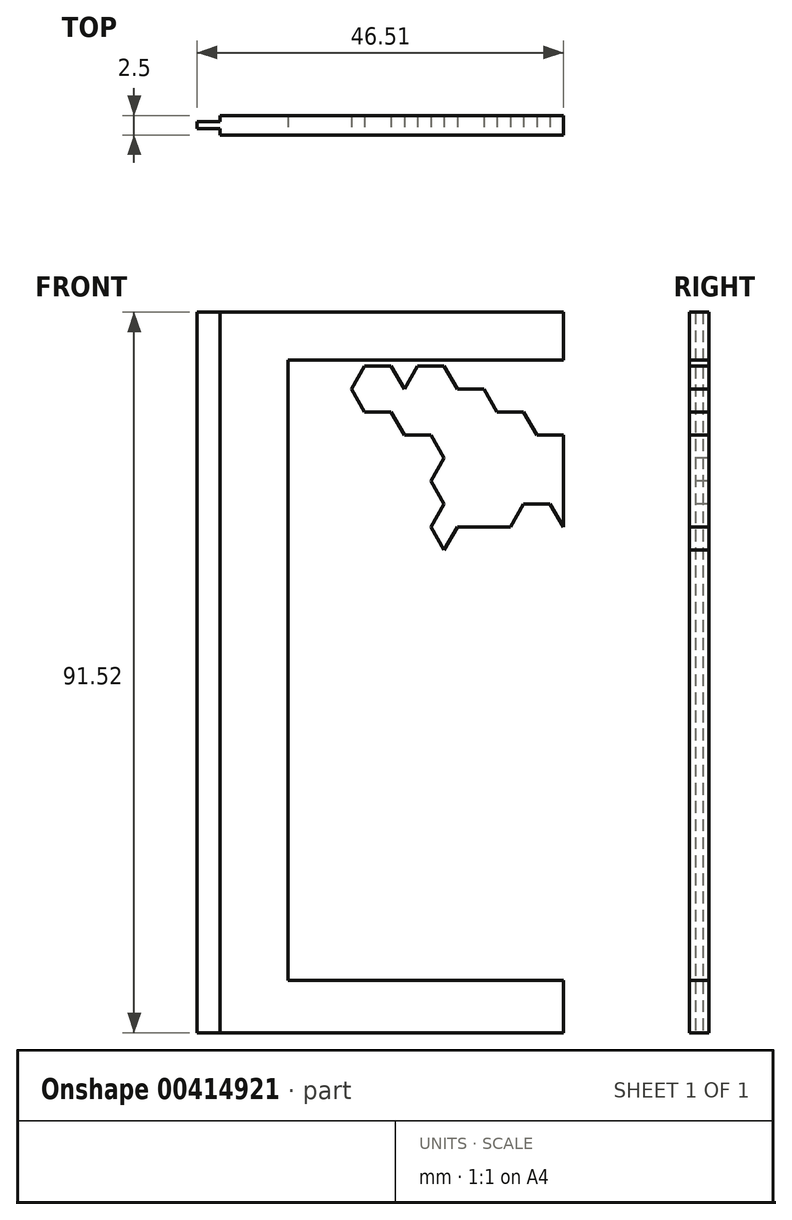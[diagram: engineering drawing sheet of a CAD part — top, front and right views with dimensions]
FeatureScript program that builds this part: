
annotation { "Feature Type Name" : "Feature", "Feature Type Description" : "" }
export const myFeature = defineFeature(function(context is Context, id is Id, definition is map)
    precondition{}
    {
        {
            var Q0;
            Q0=qCreatedBy(makeId("Front.planeOp"),FACE);
            var sketch = newSketch(context, id + "F0", { "sketchPlane" : qUnion([Q0])});
            skLineSegment(sketch, "E0.bottom", {"start": v(-43.61, 45.76) * mm, "end": v(0, 45.76) * mm});
            skLineSegment(sketch, "E0.top", {"start": v(-43.61, -45.76) * mm, "end": v(0, -45.76) * mm});
            skLineSegment(sketch, "E0.left", {"start": v(-43.61, 45.76) * mm, "end": v(-43.61, -45.76) * mm});
            skLineSegment(sketch, "E0.right", {"start": v(0, 45.76) * mm, "end": v(0, -45.76) * mm});
            skSolve(sketch);
        }
        {
            var Q0;
            Q0=makeQuery(id+"F0.imprint","IMPRINT",FACE,{"disambiguationData":[TD([[makeQuery(id+"F0.imprint","IMPRINT",EDGE,{"derivedFrom":sQuery(id+"F0.wireOp",EDGE,"E0.bottom")}),-1.0]])]});
            extrude(context, id + "F1", {"entities" : qUnion([Q0]), "oppositeDirection" : true, "depth" : 2.5 * mm});
        }
        {
            var Q0;
            Q0=makeQuery(id+"F1.opExtrude","SWEPT_FACE",FACE,{"disambiguationData":[OSD([sQuery(id+"F0.wireOp",EDGE,"E0.left")])]});
            var sketch = newSketch(context, id + "F2", { "sketchPlane" : qUnion([Q0])});
            skLineSegment(sketch, "E1.bottom", {"start": v(-0.8, 45.76) * mm, "end": v(-1.7, 45.76) * mm});
            skLineSegment(sketch, "E1.top", {"start": v(-0.8, -45.76) * mm, "end": v(-1.7, -45.76) * mm});
            skLineSegment(sketch, "E1.left", {"start": v(-0.8, 45.76) * mm, "end": v(-0.8, -45.76) * mm});
            skLineSegment(sketch, "E1.right", {"start": v(-1.7, 45.76) * mm, "end": v(-1.7, -45.76) * mm});
            skLineSegment(sketch, "E2", {"start": v(-2.5, -45.76) * mm, "end": v(-1.7, -45.76) * mm, "construction": true});
            skLineSegment(sketch, "E3", {"start": v(-0.8, -45.76) * mm, "end": v(0, -45.76) * mm, "construction": true});
            skSolve(sketch);
        }
        {
            var Q0;
            Q0=makeQuery(id+"F2.imprint","IMPRINT",FACE,{"disambiguationData":[TD([[makeQuery(id+"F2.imprint","IMPRINT",EDGE,{"derivedFrom":sQuery(id+"F2.wireOp",EDGE,"E1.bottom")}),-1.0]])]});
            extrude(context, id + "F3", {"entities" : qUnion([Q0]), "operationType" : NewBodyOperationType.ADD, "depth" : 2.9 * mm});
        }
        {
            var Q0;
            Q0=makeQuery(id+"F1.opExtrude","CAP_FACE",FACE,{"disambiguationData":[OSD([sQuery(id+"F0.wireOp",EDGE,"E0.bottom"),sQuery(id+"F0.wireOp",EDGE,"E0.top"),sQuery(id+"F0.wireOp",EDGE,"E0.left"),sQuery(id+"F0.wireOp",EDGE,"E0.right")])],"isStart":true});
            var sketch = newSketch(context, id + "F4", { "sketchPlane" : qUnion([Q0])});
            skLineSegment(sketch, "E4.bottom", {"start": v(0, 39.65) * mm, "end": v(-34.96, 39.65) * mm});
            skLineSegment(sketch, "E4.top", {"start": v(0, -39.14) * mm, "end": v(-34.96, -39.14) * mm});
            skLineSegment(sketch, "E4.left", {"start": v(0, 39.65) * mm, "end": v(0, -39.14) * mm});
            skLineSegment(sketch, "E4.right", {"start": v(-34.96, 39.65) * mm, "end": v(-34.96, -39.14) * mm});
            skLineSegment(sketch, "E5", {"start": v(0, 24.32) * mm, "end": v(0, 21.4) * mm});
            skLineSegment(sketch, "E6", {"start": v(-1.68, 21.4) * mm, "end": v(0, 24.32) * mm});
            skLineSegment(sketch, "E7.MirrorCS", {"start": v(0, 18.49) * mm, "end": v(0, 21.4) * mm});
            skLineSegment(sketch, "E8.MirrorCS", {"start": v(0, 3.16) * mm, "end": v(0, 81.95) * mm});
            skLineSegment(sketch, "E9.MirrorCS", {"start": v(-1.68, 21.4) * mm, "end": v(0, 18.49) * mm});
            skLineSegment(sketch, "E10.MirrorCS", {"start": v(-1.68, 21.4) * mm, "end": v(-5.05, 21.4) * mm});
            skLineSegment(sketch, "E11.MirrorCS", {"start": v(-5.05, 21.4) * mm, "end": v(-2.53, 22.86) * mm});
            skLineSegment(sketch, "E12.MirrorCS", {"start": v(0, 24.32) * mm, "end": v(-2.53, 22.86) * mm});
            skLineSegment(sketch, "E13.MirrorCS", {"start": v(-3.37, 24.32) * mm, "end": v(-5.05, 21.4) * mm});
            skLineSegment(sketch, "E14.MirrorCS", {"start": v(-3.37, 24.32) * mm, "end": v(0, 24.32) * mm});
            skLineSegment(sketch, "E15.MirrorCS", {"start": v(-3.37, 24.32) * mm, "end": v(-5.05, 27.24) * mm});
            skLineSegment(sketch, "E16.MirrorCS", {"start": v(-5.05, 27.24) * mm, "end": v(-2.53, 25.78) * mm});
            skLineSegment(sketch, "E17.MirrorCS", {"start": v(0, 24.32) * mm, "end": v(-2.53, 25.78) * mm});
            skLineSegment(sketch, "E18.MirrorCS", {"start": v(-1.68, 27.24) * mm, "end": v(0, 24.32) * mm});
            skLineSegment(sketch, "E19.MirrorCS", {"start": v(-1.68, 27.24) * mm, "end": v(-5.05, 27.24) * mm});
            skLineSegment(sketch, "E20.MirrorCS", {"start": v(-1.68, 27.24) * mm, "end": v(0, 30.16) * mm});
            skLineSegment(sketch, "E21.MirrorCS", {"start": v(0, 45.49) * mm, "end": v(0, -33.3) * mm});
            skLineSegment(sketch, "E22.MirrorCS", {"start": v(0, 30.16) * mm, "end": v(0, 27.24) * mm});
            skLineSegment(sketch, "E23.MirrorCS", {"start": v(-5.05, 27.24) * mm, "end": v(-5.05, 24.32) * mm});
            skLineSegment(sketch, "E24.MirrorCS", {"start": v(-5.05, 21.4) * mm, "end": v(-5.05, 24.32) * mm});
            skLineSegment(sketch, "E25.MirrorCS", {"start": v(-6.74, 24.32) * mm, "end": v(-5.05, 27.24) * mm});
            skLineSegment(sketch, "E26.MirrorCS", {"start": v(-6.74, 24.32) * mm, "end": v(-5.05, 21.4) * mm});
            skLineSegment(sketch, "E27.MirrorCS", {"start": v(-6.74, 24.32) * mm, "end": v(-10.1, 24.32) * mm});
            skLineSegment(sketch, "E28.MirrorCS", {"start": v(-10.1, 24.32) * mm, "end": v(-7.58, 25.78) * mm});
            skLineSegment(sketch, "E29.MirrorCS", {"start": v(-5.05, 27.24) * mm, "end": v(-7.58, 25.78) * mm});
            skLineSegment(sketch, "E30.MirrorCS", {"start": v(-8.42, 27.24) * mm, "end": v(-5.05, 27.24) * mm});
            skLineSegment(sketch, "E31.MirrorCS", {"start": v(-5.05, 27.24) * mm, "end": v(-7.58, 28.7) * mm});
            skLineSegment(sketch, "E32.MirrorCS", {"start": v(-10.1, 30.16) * mm, "end": v(-7.58, 28.7) * mm});
            skLineSegment(sketch, "E33.MirrorCS", {"start": v(-6.74, 30.16) * mm, "end": v(-5.05, 27.24) * mm});
            skLineSegment(sketch, "E34.MirrorCS", {"start": v(-6.74, 30.16) * mm, "end": v(-10.1, 30.16) * mm});
            skLineSegment(sketch, "E35.MirrorCS", {"start": v(-10.1, 30.16) * mm, "end": v(-10.1, 27.24) * mm});
            skLineSegment(sketch, "E36.MirrorCS", {"start": v(-10.1, 24.32) * mm, "end": v(-10.1, 27.24) * mm});
            skLineSegment(sketch, "E37.MirrorCS", {"start": v(-8.42, 27.24) * mm, "end": v(-10.1, 24.32) * mm});
            skLineSegment(sketch, "E38.MirrorCS", {"start": v(-8.42, 27.24) * mm, "end": v(-10.1, 30.16) * mm});
            skLineSegment(sketch, "E39.MirrorCS", {"start": v(-11.79, 27.24) * mm, "end": v(-15.15, 27.24) * mm});
            skLineSegment(sketch, "E40.MirrorCS", {"start": v(-11.79, 27.24) * mm, "end": v(-10.1, 30.16) * mm});
            skLineSegment(sketch, "E41.MirrorCS", {"start": v(-11.79, 27.24) * mm, "end": v(-10.1, 24.32) * mm});
            skLineSegment(sketch, "E42.MirrorCS", {"start": v(-15.15, 27.24) * mm, "end": v(-12.63, 28.7) * mm});
            skLineSegment(sketch, "E43.MirrorCS", {"start": v(-11.79, 33.07) * mm, "end": v(-10.1, 30.16) * mm});
            skLineSegment(sketch, "E44.MirrorCS", {"start": v(-11.79, 33.07) * mm, "end": v(-15.15, 33.07) * mm});
            skLineSegment(sketch, "E45.MirrorCS", {"start": v(-16.84, 35.99) * mm, "end": v(-15.15, 33.07) * mm});
            skLineSegment(sketch, "E46.MirrorCS", {"start": v(-16.84, 35.99) * mm, "end": v(-20.2, 35.99) * mm});
            skLineSegment(sketch, "E47.MirrorCS", {"start": v(-21.89, 33.07) * mm, "end": v(-20.2, 35.99) * mm});
            skLineSegment(sketch, "E48.MirrorCS", {"start": v(-21.89, 33.07) * mm, "end": v(-20.2, 30.16) * mm});
            skLineSegment(sketch, "E49.MirrorCS", {"start": v(-18.52, 33.07) * mm, "end": v(-20.2, 35.99) * mm});
            skLineSegment(sketch, "E50.MirrorCS", {"start": v(-18.52, 33.07) * mm, "end": v(-20.2, 30.16) * mm});
            skLineSegment(sketch, "E51.MirrorCS", {"start": v(-18.52, 33.07) * mm, "end": v(-15.15, 33.07) * mm});
            skLineSegment(sketch, "E52.MirrorCS", {"start": v(-20.2, 30.16) * mm, "end": v(-17.68, 31.61) * mm});
            skLineSegment(sketch, "E53.MirrorCS", {"start": v(-15.15, 33.07) * mm, "end": v(-17.68, 31.61) * mm});
            skLineSegment(sketch, "E54.MirrorCS", {"start": v(-16.84, 30.16) * mm, "end": v(-20.2, 30.16) * mm});
            skLineSegment(sketch, "E55.MirrorCS", {"start": v(-16.84, 30.16) * mm, "end": v(-15.15, 33.07) * mm});
            skLineSegment(sketch, "E56.MirrorCS", {"start": v(-16.84, 30.16) * mm, "end": v(-15.15, 27.24) * mm});
            skLineSegment(sketch, "E57.MirrorCS", {"start": v(-15.15, 33.07) * mm, "end": v(-15.15, 30.16) * mm});
            skLineSegment(sketch, "E58.MirrorCS", {"start": v(-15.15, 27.24) * mm, "end": v(-15.15, 30.16) * mm});
            skLineSegment(sketch, "E59.MirrorCS", {"start": v(-13.47, 30.16) * mm, "end": v(-15.15, 27.24) * mm});
            skLineSegment(sketch, "E60.MirrorCS", {"start": v(-13.47, 30.16) * mm, "end": v(-15.15, 33.07) * mm});
            skLineSegment(sketch, "E61.MirrorCS", {"start": v(-13.47, 30.16) * mm, "end": v(-10.1, 30.16) * mm});
            skLineSegment(sketch, "E62.MirrorCS", {"start": v(-10.1, 30.16) * mm, "end": v(-12.63, 28.7) * mm});
            skLineSegment(sketch, "E63.MirrorCS", {"start": v(-10.1, 30.16) * mm, "end": v(-12.63, 31.61) * mm});
            skLineSegment(sketch, "E64.MirrorCS", {"start": v(-15.15, 33.07) * mm, "end": v(-12.63, 31.61) * mm});
            skLineSegment(sketch, "E65.MirrorCS", {"start": v(-15.15, 33.07) * mm, "end": v(-17.68, 34.53) * mm});
            skLineSegment(sketch, "E66.MirrorCS", {"start": v(-20.2, 35.99) * mm, "end": v(-17.68, 34.53) * mm});
            skLineSegment(sketch, "E67.MirrorCS", {"start": v(-20.2, 35.99) * mm, "end": v(-20.2, 33.07) * mm});
            skLineSegment(sketch, "E68.MirrorCS", {"start": v(-20.2, 30.16) * mm, "end": v(-20.2, 33.07) * mm});
            skLineSegment(sketch, "E69.MirrorCS", {"start": v(-18.52, 38.9) * mm, "end": v(-20.2, 35.99) * mm});
            skLineSegment(sketch, "E70.MirrorCS", {"start": v(-18.52, 38.9) * mm, "end": v(-15.15, 38.9) * mm});
            skLineSegment(sketch, "E71.MirrorCS", {"start": v(-13.47, 35.99) * mm, "end": v(-15.15, 38.9) * mm});
            skLineSegment(sketch, "E72.MirrorCS", {"start": v(-13.47, 35.99) * mm, "end": v(-10.1, 35.99) * mm});
            skLineSegment(sketch, "E73.MirrorCS", {"start": v(-8.42, 33.07) * mm, "end": v(-10.1, 35.99) * mm});
            skLineSegment(sketch, "E74.MirrorCS", {"start": v(-8.42, 33.07) * mm, "end": v(-5.05, 33.07) * mm});
            skLineSegment(sketch, "E75.MirrorCS", {"start": v(-3.37, 30.16) * mm, "end": v(-5.05, 33.07) * mm});
            skLineSegment(sketch, "E76.MirrorCS", {"start": v(-3.37, 30.16) * mm, "end": v(0, 30.16) * mm});
            skLineSegment(sketch, "E77.MirrorCS", {"start": v(-20.2, 35.99) * mm, "end": v(-17.68, 37.45) * mm});
            skLineSegment(sketch, "E78.MirrorCS", {"start": v(-15.15, 38.9) * mm, "end": v(-17.68, 37.45) * mm});
            skLineSegment(sketch, "E79.MirrorCS", {"start": v(-16.84, 35.99) * mm, "end": v(-15.15, 38.9) * mm});
            skLineSegment(sketch, "E80.MirrorCS", {"start": v(-15.15, 38.9) * mm, "end": v(-15.15, 35.99) * mm});
            skLineSegment(sketch, "E81.MirrorCS", {"start": v(-15.15, 33.07) * mm, "end": v(-15.15, 35.99) * mm});
            skLineSegment(sketch, "E82.MirrorCS", {"start": v(-13.47, 35.99) * mm, "end": v(-15.15, 33.07) * mm});
            skLineSegment(sketch, "E83.MirrorCS", {"start": v(-15.15, 33.07) * mm, "end": v(-12.63, 34.53) * mm});
            skLineSegment(sketch, "E84.MirrorCS", {"start": v(-10.1, 35.99) * mm, "end": v(-12.63, 34.53) * mm});
            skLineSegment(sketch, "E85.MirrorCS", {"start": v(-11.79, 33.07) * mm, "end": v(-10.1, 35.99) * mm});
            skLineSegment(sketch, "E86.MirrorCS", {"start": v(-10.1, 35.99) * mm, "end": v(-10.1, 33.07) * mm});
            skLineSegment(sketch, "E87.MirrorCS", {"start": v(-10.1, 30.16) * mm, "end": v(-10.1, 33.07) * mm});
            skLineSegment(sketch, "E88.MirrorCS", {"start": v(-8.42, 33.07) * mm, "end": v(-10.1, 30.16) * mm});
            skLineSegment(sketch, "E89.MirrorCS", {"start": v(-10.1, 30.16) * mm, "end": v(-7.58, 31.61) * mm});
            skLineSegment(sketch, "E90.MirrorCS", {"start": v(-5.05, 33.07) * mm, "end": v(-7.58, 31.61) * mm});
            skLineSegment(sketch, "E91.MirrorCS", {"start": v(-6.74, 30.16) * mm, "end": v(-5.05, 33.07) * mm});
            skLineSegment(sketch, "E92.MirrorCS", {"start": v(-5.05, 33.07) * mm, "end": v(-5.05, 30.16) * mm});
            skLineSegment(sketch, "E93.MirrorCS", {"start": v(-5.05, 27.24) * mm, "end": v(-5.05, 30.16) * mm});
            skLineSegment(sketch, "E94.MirrorCS", {"start": v(-3.37, 30.16) * mm, "end": v(-5.05, 27.24) * mm});
            skLineSegment(sketch, "E95.MirrorCS", {"start": v(-5.05, 27.24) * mm, "end": v(-2.53, 28.7) * mm});
            skLineSegment(sketch, "E96.MirrorCS", {"start": v(0, 30.16) * mm, "end": v(-2.53, 28.7) * mm});
            skLineSegment(sketch, "E97.MirrorCS", {"start": v(-21.89, 33.07) * mm, "end": v(-25.26, 33.07) * mm});
            skLineSegment(sketch, "E98.MirrorCS", {"start": v(-26.94, 35.99) * mm, "end": v(-25.26, 33.07) * mm});
            skLineSegment(sketch, "E99.MirrorCS", {"start": v(-26.94, 35.99) * mm, "end": v(-25.26, 38.9) * mm});
            skLineSegment(sketch, "E100.MirrorCS", {"start": v(-25.26, 38.9) * mm, "end": v(-22.73, 37.45) * mm});
            skLineSegment(sketch, "E101.MirrorCS", {"start": v(-20.2, 35.99) * mm, "end": v(-22.73, 37.45) * mm});
            skLineSegment(sketch, "E102.MirrorCS", {"start": v(-21.89, 38.9) * mm, "end": v(-20.2, 35.99) * mm});
            skLineSegment(sketch, "E103.MirrorCS", {"start": v(-21.89, 38.9) * mm, "end": v(-25.26, 38.9) * mm});
            skLineSegment(sketch, "E104.MirrorCS", {"start": v(-25.26, 38.9) * mm, "end": v(-25.26, 35.99) * mm});
            skLineSegment(sketch, "E105.MirrorCS", {"start": v(-25.26, 33.07) * mm, "end": v(-25.26, 35.99) * mm});
            skLineSegment(sketch, "E106.MirrorCS", {"start": v(-23.57, 35.99) * mm, "end": v(-25.26, 33.07) * mm});
            skLineSegment(sketch, "E107.MirrorCS", {"start": v(-23.57, 35.99) * mm, "end": v(-20.2, 35.99) * mm});
            skLineSegment(sketch, "E108.MirrorCS", {"start": v(-20.2, 35.99) * mm, "end": v(-22.73, 34.53) * mm});
            skLineSegment(sketch, "E109.MirrorCS", {"start": v(-25.26, 33.07) * mm, "end": v(-22.73, 34.53) * mm});
            skLineSegment(sketch, "E110.MirrorCS", {"start": v(-20.2, 35.99) * mm, "end": v(-20.2, 38.9) * mm});
            skLineSegment(sketch, "E111.MirrorCS", {"start": v(-10.1, 24.32) * mm, "end": v(-10.1, 21.4) * mm});
            skLineSegment(sketch, "E112.MirrorCS", {"start": v(-10.1, 18.49) * mm, "end": v(-10.1, 21.4) * mm});
            skLineSegment(sketch, "E113.MirrorCS", {"start": v(-6.74, 18.49) * mm, "end": v(-10.1, 18.49) * mm});
            skLineSegment(sketch, "E114.MirrorCS", {"start": v(-6.74, 18.49) * mm, "end": v(-5.05, 15.57) * mm});
            skLineSegment(sketch, "E115.MirrorCS", {"start": v(-6.74, 18.49) * mm, "end": v(-5.05, 21.4) * mm});
            skLineSegment(sketch, "E116.MirrorCS", {"start": v(-5.05, 21.4) * mm, "end": v(-7.58, 19.95) * mm});
            skLineSegment(sketch, "E117.MirrorCS", {"start": v(-10.1, 18.49) * mm, "end": v(-7.58, 19.95) * mm});
            skLineSegment(sketch, "E118.MirrorCS", {"start": v(-8.42, 21.4) * mm, "end": v(-5.05, 21.4) * mm});
            skLineSegment(sketch, "E119.MirrorCS", {"start": v(-8.42, 21.4) * mm, "end": v(-10.1, 24.32) * mm});
            skLineSegment(sketch, "E120.MirrorCS", {"start": v(-8.42, 21.4) * mm, "end": v(-10.1, 18.49) * mm});
            skLineSegment(sketch, "E121.MirrorCS", {"start": v(-10.1, 24.32) * mm, "end": v(-7.58, 22.86) * mm});
            skLineSegment(sketch, "E122.MirrorCS", {"start": v(-5.05, 21.4) * mm, "end": v(-7.58, 22.86) * mm});
            skLineSegment(sketch, "E123.MirrorCS", {"start": v(-5.05, 15.57) * mm, "end": v(-7.58, 17.03) * mm});
            skLineSegment(sketch, "E124.MirrorCS", {"start": v(-11.79, 21.4) * mm, "end": v(-10.1, 18.49) * mm});
            skLineSegment(sketch, "E125.MirrorCS", {"start": v(-11.79, 21.4) * mm, "end": v(-10.1, 24.32) * mm});
            skLineSegment(sketch, "E126.MirrorCS", {"start": v(-10.1, 24.32) * mm, "end": v(-12.63, 22.86) * mm});
            skLineSegment(sketch, "E127.MirrorCS", {"start": v(-15.15, 21.4) * mm, "end": v(-12.63, 22.86) * mm});
            skLineSegment(sketch, "E128.MirrorCS", {"start": v(-11.79, 21.4) * mm, "end": v(-15.15, 21.4) * mm});
            skLineSegment(sketch, "E129.MirrorCS", {"start": v(-15.15, 21.4) * mm, "end": v(-12.63, 19.95) * mm});
            skLineSegment(sketch, "E130.MirrorCS", {"start": v(-10.1, 18.49) * mm, "end": v(-12.63, 19.95) * mm});
            skLineSegment(sketch, "E131.MirrorCS", {"start": v(-13.47, 18.49) * mm, "end": v(-15.15, 21.4) * mm});
            skLineSegment(sketch, "E132.MirrorCS", {"start": v(-13.47, 18.49) * mm, "end": v(-10.1, 18.49) * mm});
            skLineSegment(sketch, "E133.MirrorCS", {"start": v(-13.47, 18.49) * mm, "end": v(-15.15, 15.57) * mm});
            skLineSegment(sketch, "E134.MirrorCS", {"start": v(-15.15, 15.57) * mm, "end": v(-12.63, 17.03) * mm});
            skLineSegment(sketch, "E135.MirrorCS", {"start": v(-13.47, 24.32) * mm, "end": v(-10.1, 24.32) * mm});
            skLineSegment(sketch, "E136.MirrorCS", {"start": v(-13.47, 24.32) * mm, "end": v(-15.15, 21.4) * mm});
            skLineSegment(sketch, "E137.MirrorCS", {"start": v(-15.15, 21.4) * mm, "end": v(-15.15, 24.32) * mm});
            skLineSegment(sketch, "E138.MirrorCS", {"start": v(-15.15, 27.24) * mm, "end": v(-15.15, 24.32) * mm});
            skLineSegment(sketch, "E139.MirrorCS", {"start": v(-15.15, 27.24) * mm, "end": v(-12.63, 25.78) * mm});
            skLineSegment(sketch, "E140.MirrorCS", {"start": v(-10.1, 24.32) * mm, "end": v(-12.63, 25.78) * mm});
            skLineSegment(sketch, "E141.MirrorCS", {"start": v(-13.47, 24.32) * mm, "end": v(-15.15, 27.24) * mm});
            skLineSegment(sketch, "E142.MirrorCS", {"start": v(-16.84, 24.32) * mm, "end": v(-15.15, 27.24) * mm});
            skLineSegment(sketch, "E143.MirrorCS", {"start": v(-16.84, 24.32) * mm, "end": v(-15.15, 21.4) * mm});
            skLineSegment(sketch, "E144.MirrorCS", {"start": v(-16.84, 18.49) * mm, "end": v(-15.15, 21.4) * mm});
            skLineSegment(sketch, "E145.MirrorCS", {"start": v(-15.15, 21.4) * mm, "end": v(-15.15, 18.49) * mm});
            skLineSegment(sketch, "E146.MirrorCS", {"start": v(-15.15, 15.57) * mm, "end": v(-15.15, 18.49) * mm});
            skLineSegment(sketch, "E147.MirrorCS", {"start": v(-16.84, 18.49) * mm, "end": v(-15.15, 15.57) * mm});
            skSolve(sketch);
        }
        {
            var Q0;
            Q0=makeQuery(id+"F4.imprint","IMPRINT",FACE,{"disambiguationData":[TD([[makeQuery(id+"F4.imprint","IMPRINT",EDGE,{"derivedFrom":sQuery(id+"F4.wireOp",EDGE,"E4.bottom")}),1.0]])]});
            extrude(context, id + "F5", {"entities" : qUnion([Q0]), "operationType" : NewBodyOperationType.REMOVE, "endBound" : BoundingType.UP_TO_NEXT, "oppositeDirection" : true, "depth" : 25 * mm});
        }
    });
